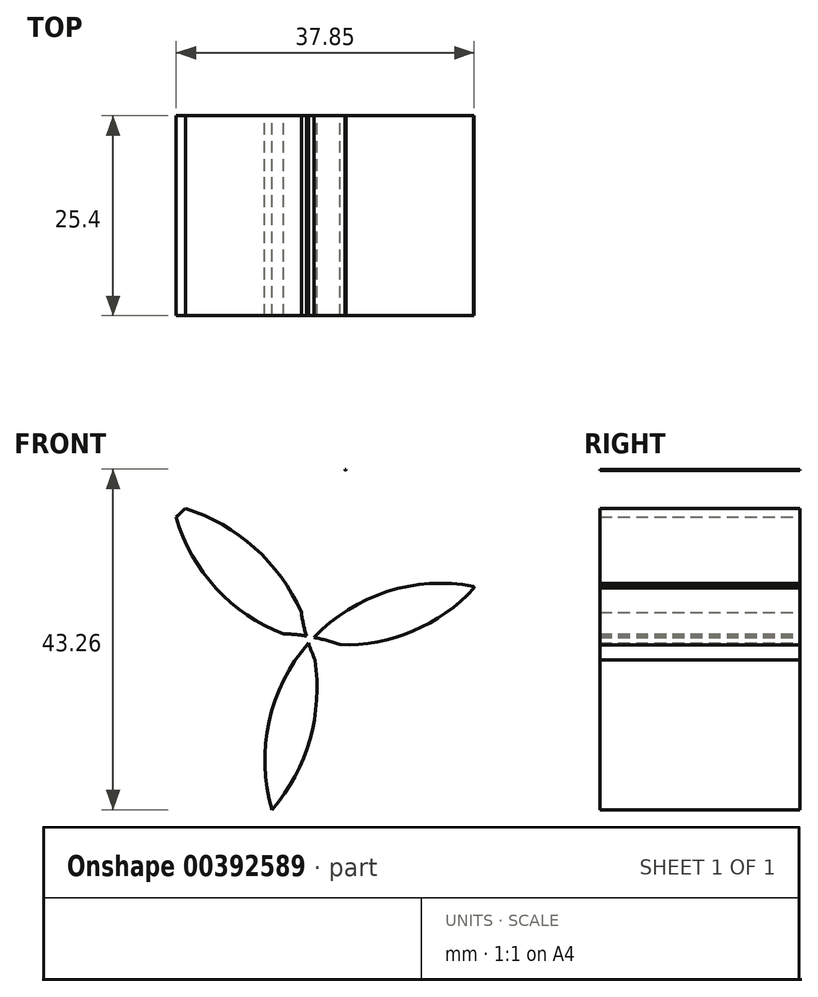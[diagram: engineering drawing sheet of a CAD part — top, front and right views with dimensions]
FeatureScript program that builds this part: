
annotation { "Feature Type Name" : "Feature", "Feature Type Description" : "" }
export const myFeature = defineFeature(function(context is Context, id is Id, definition is map)
    precondition{}
    {
        {
            var Q0;
            Q0=qCreatedBy(makeId("Front.planeOp"),FACE);
            var sketch = newSketch(context, id + "F0", { "sketchPlane" : qUnion([Q0])});
            skCircle(sketch, "E0", {"center": v(0, 0) * mm, "radius": 22.82 * mm});
            skCircle(sketch, "E1", {"center": v(-16.23, 16.03) * mm, "radius": 22.38 * mm});
            skCircle(sketch, "E2", {"center": v(5.29, 22.2) * mm, "radius": 22.3 * mm});
            skCircle(sketch, "E3", {"center": v(21.69, 7.1) * mm, "radius": 22.16 * mm});
            skCircle(sketch, "E4", {"center": v(17.48, -14.67) * mm, "radius": 22.38 * mm});
            skCircle(sketch, "E5", {"center": v(-22.13, -5.56) * mm, "radius": 23.87 * mm});
            skCircle(sketch, "E6", {"center": v(-3.47, -22.55) * mm, "radius": 23.87 * mm});
            skSolve(sketch);
        }
        {
            var Q0;
            {var subQ3=sQuery(id+"F0.wireOp",EDGE,"E5");var subQ5=sQuery(id+"F0.wireOp",EDGE,"E0");var subQ6=makeQuery(id+"F0.imprint","INTERSECT",VERTEX,{"disambiguationData":[OD(0.0)],"derivedFrom":[subQ5,subQ3]});Q0=makeQuery(id+"F0.imprint","IMPRINT",FACE,{"disambiguationData":[TD([[makeQuery(id+"F0.imprint","IMPRINT",EDGE,{"disambiguationData":[TD([[subQ6,-1.0]])],"derivedFrom":subQ5}),1.0]])]});}
            var Q1;
            {var subQ0=sQuery(id+"F0.wireOp",EDGE,"E3");var subQ1=sQuery(id+"F0.wireOp",EDGE,"E1");var subQ2=makeQuery(id+"F0.imprint","INTERSECT",VERTEX,{"disambiguationData":[OD(0.0)],"derivedFrom":[subQ1,subQ0]});Q1=makeQuery(id+"F0.imprint","IMPRINT",FACE,{"disambiguationData":[TD([[makeQuery(id+"F0.imprint","IMPRINT",EDGE,{"disambiguationData":[TD([[subQ2,1.0]])],"derivedFrom":subQ1}),1.0]])]});}
            var Q2;
            {var subQ0=sQuery(id+"F0.wireOp",EDGE,"E4");var subQ1=sQuery(id+"F0.wireOp",EDGE,"E0");var subQ2=makeQuery(id+"F0.imprint","INTERSECT",VERTEX,{"disambiguationData":[OD(0.0)],"derivedFrom":[subQ1,subQ0]});Q2=makeQuery(id+"F0.imprint","IMPRINT",FACE,{"disambiguationData":[TD([[makeQuery(id+"F0.imprint","IMPRINT",EDGE,{"disambiguationData":[TD([[subQ2,1.0]])],"derivedFrom":subQ1}),1.0]])]});}
            var Q3;
            {var subQ3=sQuery(id+"F0.wireOp",EDGE,"E3");var subQ5=sQuery(id+"F0.wireOp",EDGE,"E0");var subQ6=makeQuery(id+"F0.imprint","INTERSECT",VERTEX,{"disambiguationData":[OD(1.0)],"derivedFrom":[subQ5,subQ3]});Q3=makeQuery(id+"F0.imprint","IMPRINT",FACE,{"disambiguationData":[TD([[makeQuery(id+"F0.imprint","IMPRINT",EDGE,{"disambiguationData":[TD([[subQ6,-1.0]])],"derivedFrom":subQ5}),1.0]])]});}
            var Q4;
            {var subQ0=sQuery(id+"F0.wireOp",EDGE,"E4");var subQ1=sQuery(id+"F0.wireOp",EDGE,"E3");var subQ2=makeQuery(id+"F0.imprint","INTERSECT",VERTEX,{"disambiguationData":[OD(1.0)],"derivedFrom":[subQ1,subQ0]});Q4=makeQuery(id+"F0.imprint","IMPRINT",FACE,{"disambiguationData":[TD([[makeQuery(id+"F0.imprint","IMPRINT",EDGE,{"disambiguationData":[TD([[subQ2,-1.0]])],"derivedFrom":subQ1}),-1.0]])]});}
            var Q5;
            {var subQ0=sQuery(id+"F0.wireOp",EDGE,"E6");var subQ1=sQuery(id+"F0.wireOp",EDGE,"E1");var subQ2=makeQuery(id+"F0.imprint","INTERSECT",VERTEX,{"disambiguationData":[OD(0.0)],"derivedFrom":[subQ1,subQ0]});Q5=makeQuery(id+"F0.imprint","IMPRINT",FACE,{"disambiguationData":[TD([[makeQuery(id+"F0.imprint","IMPRINT",EDGE,{"disambiguationData":[TD([[subQ2,-1.0]])],"derivedFrom":subQ1}),1.0]])]});}
            extrude(context, id + "F1", {"entities" : qUnion([Q0, Q1, Q2, Q3, Q4, Q5]), "depth" : 25.4 * mm});
        }
    });
